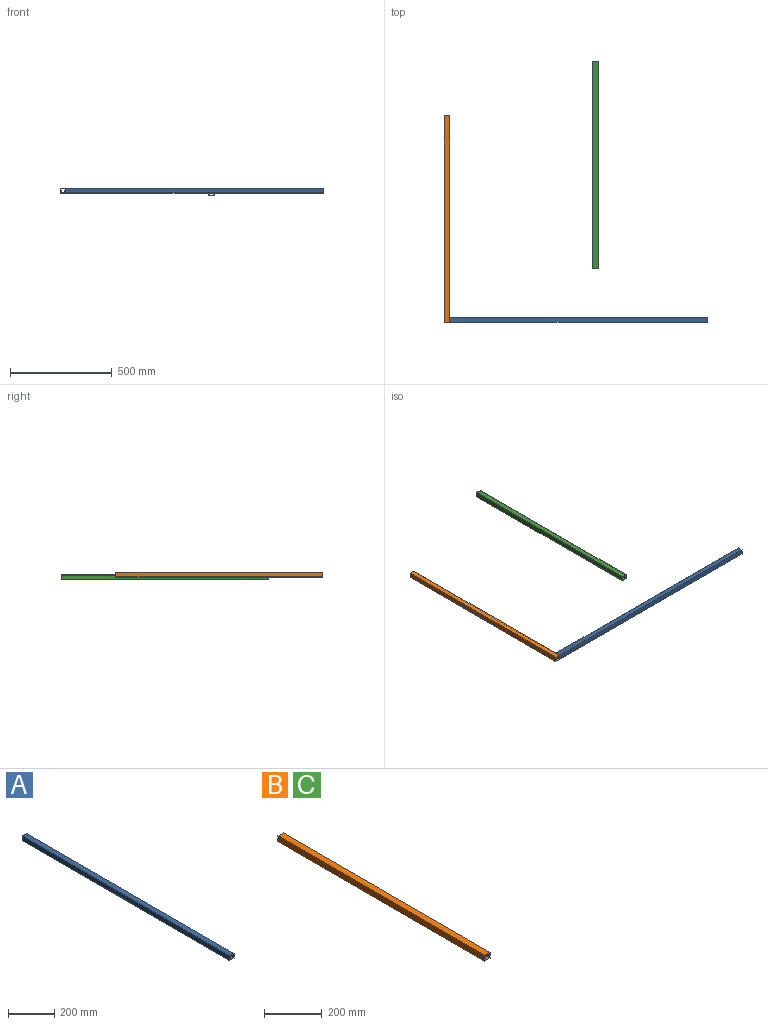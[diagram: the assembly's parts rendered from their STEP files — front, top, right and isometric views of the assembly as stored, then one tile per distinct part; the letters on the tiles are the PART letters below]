
ASSEMBLY  parts=3 mates=1
PART A: 10 faces, bbox 25.4x1270x25.4 mm
  f0: plane 1270x25.4mm, normal (0,0,1), area 32258mm2, adj f1,f7,f8,f9
  f1: plane 1270x25.4mm, normal (-1,0,0), area 32258mm2, adj f0,f2,f8,f9
  f2: plane 1270x25.4mm, normal (0,0,-1), area 32258mm2, adj f1,f7,f8,f9
  f3: plane 1270x19.05mm, normal (0,0,1), area 24193.5mm2, adj f4,f6,f8,f9
  f4: plane 1270x19.05mm, normal (1,0,0), area 24193.5mm2, adj f3,f5,f8,f9
  f5: plane 1270x19.05mm, normal (0,0,-1), area 24193.5mm2, adj f4,f6,f8,f9
  f6: plane 1270x19.05mm, normal (-1,0,0), area 24193.5mm2, adj f3,f5,f8,f9
  f7: plane 1270x25.4mm, normal (1,0,0), area 32258mm2, adj f0,f2,f8,f9
  f8: plane 25.4x25.4mm, normal (0,-1,0), area 282.3mm2, adj f0,f1,f2,f3,f4,f5,f6,f7
  f9: plane 25.4x25.4mm, normal (0,1,0), area 282.3mm2, adj f0,f1,f2,f3,f4,f5,f6,f7
PART B: 10 faces, bbox 25.4x1016x25.4 mm
  f0: plane 1016x25.4mm, normal (0,0,1), area 25806.4mm2, adj f1,f7,f8,f9
  f1: plane 1016x25.4mm, normal (-1,0,0), area 25806.4mm2, adj f0,f2,f8,f9
  f2: plane 1016x25.4mm, normal (0,0,-1), area 25806.4mm2, adj f1,f7,f8,f9
  f3: plane 1016x19.05mm, normal (1,0,0), area 19354.8mm2, adj f4,f6,f8,f9
  f4: plane 1016x19.05mm, normal (0,0,-1), area 19354.8mm2, adj f3,f5,f8,f9
  f5: plane 1016x19.05mm, normal (-1,0,0), area 19354.8mm2, adj f4,f6,f8,f9
  f6: plane 1016x19.05mm, normal (0,0,1), area 19354.8mm2, adj f3,f5,f8,f9
  f7: plane 1016x25.4mm, normal (1,0,0), area 25806.4mm2, adj f0,f2,f8,f9
  f8: plane 25.4x25.4mm, normal (0,-1,0), area 282.3mm2, adj f0,f1,f2,f3,f4,f5,f6,f7
  f9: plane 25.4x25.4mm, normal (0,1,0), area 282.3mm2, adj f0,f1,f2,f3,f4,f5,f6,f7
PART C: same geometry as B
PLACE A rot(axis=(0,0,-1),90deg) t=(281.65,-667.1,59.31)mm
PLACE B t=(-366.05,-171.8,59.31)mm fixed
PLACE C t=(364.86,95.5,46.23)mm
MATE fastened A.f8 <-> B.f7  axis (-1,0,0) through (-353.35,-679.8,59.31)mm
